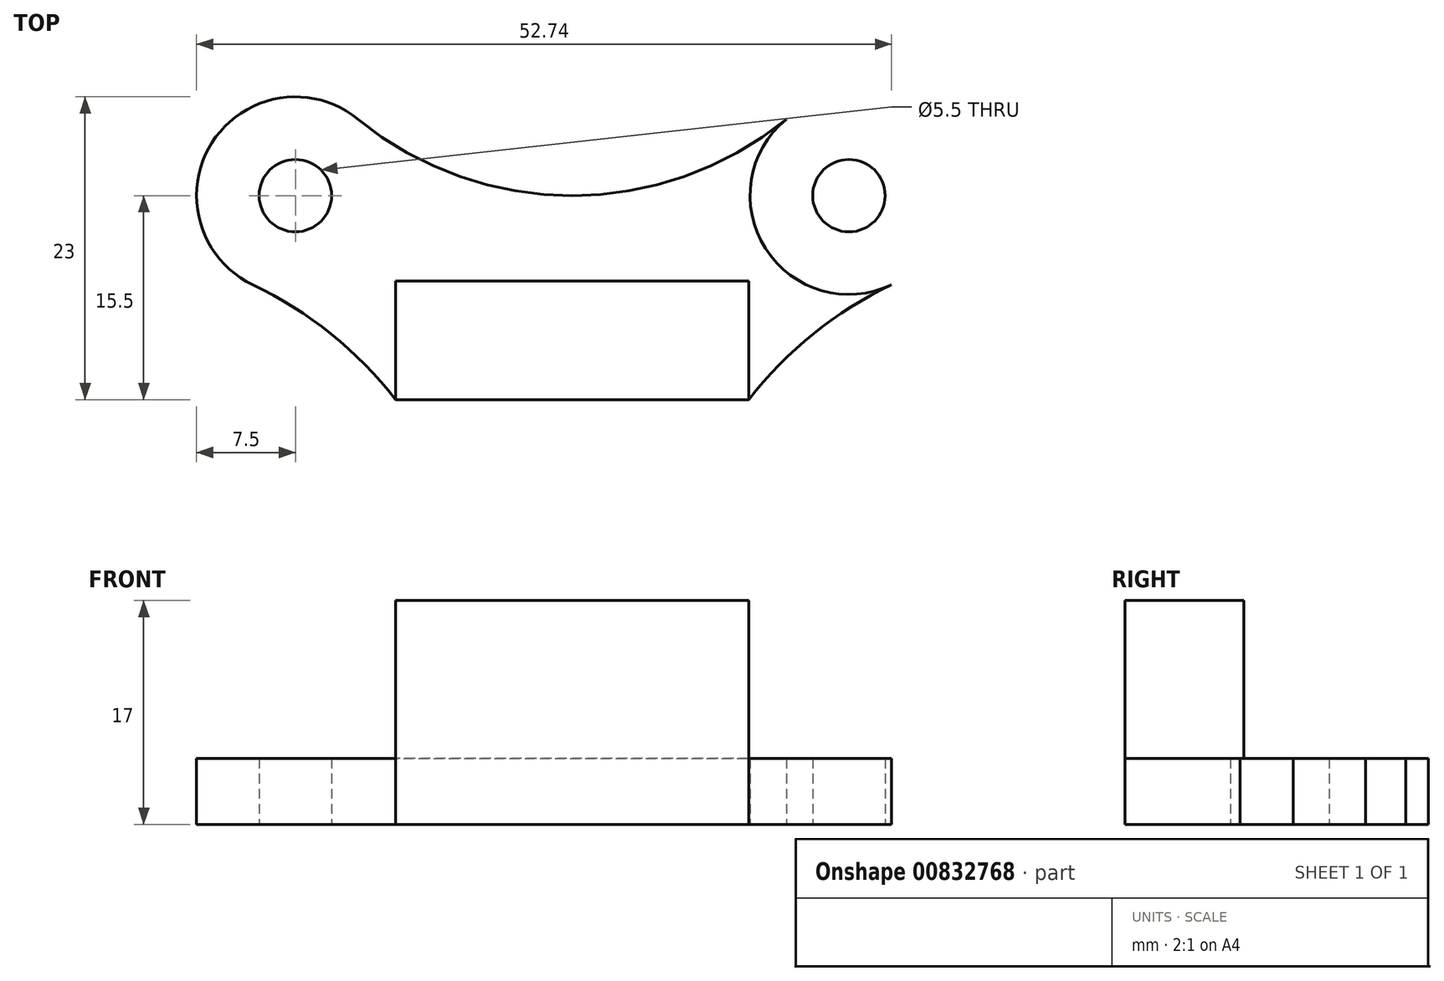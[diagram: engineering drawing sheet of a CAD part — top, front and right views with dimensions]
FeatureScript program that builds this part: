
annotation { "Feature Type Name" : "Feature", "Feature Type Description" : "" }
export const myFeature = defineFeature(function(context is Context, id is Id, definition is map)
    precondition{}
    {
        {
            var Q0;
            Q0=qCreatedBy(makeId("Top.planeOp"),FACE);
            var sketch = newSketch(context, id + "F0", { "sketchPlane" : qUnion([Q0])});
            skLineSegment(sketch, "E0", {"start": v(0, 0) * mm, "end": v(-21, 0) * mm, "construction": true});
            skLineSegment(sketch, "E1", {"start": v(0, 15.73) * mm, "end": v(0, -40) * mm, "construction": true});
            skCircle(sketch, "E2", {"center": v(-21, 0) * mm, "radius": 7.5 * mm});
            skCircle(sketch, "E3", {"center": v(-21, 0) * mm, "radius": 2.75 * mm});
            skCircle(sketch, "E4.MirrorC", {"center": v(21, 0) * mm, "radius": 7.5 * mm});
            skCircle(sketch, "E5.MirrorC", {"center": v(21, 0) * mm, "radius": 2.75 * mm});
            skLineSegment(sketch, "E6", {"start": v(-21, 0) * mm, "end": v(0, -40) * mm, "construction": true});
            skArc(sketch, "E7", {"start": v(-16.25, 5.8) * mm, "mid": v(0, 0) * mm, "end": v(16.25, 5.8) * mm});
            skCircle(sketch, "E8", {"center": v(0, -40) * mm, "radius": 7.5 * mm, "construction": true});
            skArc(sketch, "E9", {"start": v(-7.4, -38.82) * mm, "mid": v(-10.5, -20) * mm, "end": v(-24.24, -6.77) * mm});
            skArc(sketch, "E10.MirrorCS", {"start": v(7.4, -38.82) * mm, "mid": v(10.5, -20) * mm, "end": v(24.24, -6.77) * mm});
            skPoint(sketch, "E11", {"position": v(0, -6.5) * mm});
            skLineSegment(sketch, "E12", {"start": v(-13.4, -15.5) * mm, "end": v(13.4, -15.5) * mm});
            skSolve(sketch);
        }
        {
            var Q0;
            {var subQ4=sQuery(id+"F0.wireOp",EDGE,"E7");Q0=makeQuery(id+"F0.imprint","IMPRINT",FACE,{"disambiguationData":[TD([[makeQuery(id+"F0.imprint","IMPRINT",EDGE,{"derivedFrom":subQ4}),-1.0]])]});}
            var Q1;
            Q1=makeQuery(id+"F0.imprint","IMPRINT",FACE,{"disambiguationData":[TD([[makeQuery(id+"F0.imprint","IMPRINT",EDGE,{"derivedFrom":sQuery(id+"F0.wireOp",EDGE,"E3")}),-1.0]])]});
            var Q2;
            Q2=makeQuery(id+"F0.imprint","IMPRINT",FACE,{"disambiguationData":[TD([[makeQuery(id+"F0.imprint","IMPRINT",EDGE,{"derivedFrom":sQuery(id+"F0.wireOp",EDGE,"E5.MirrorC")}),1.0]])]});
            extrude(context, id + "F1", {"entities" : qUnion([Q0, Q1, Q2]), "depth" : 5 * mm, "offsetDistance" : 25 * mm});
        }
        {
            var Q0;
            Q0=makeQuery(id+"F1.opExtrude","CAP_FACE",FACE,{"disambiguationData":[OSD([sQuery(id+"F0.wireOp",EDGE,"E2"),sQuery(id+"F0.wireOp",EDGE,"E3"),sQuery(id+"F0.wireOp",EDGE,"E4.MirrorC"),sQuery(id+"F0.wireOp",EDGE,"E5.MirrorC"),sQuery(id+"F0.wireOp",EDGE,"E7"),sQuery(id+"F0.wireOp",EDGE,"E9"),sQuery(id+"F0.wireOp",EDGE,"E10.MirrorCS"),sQuery(id+"F0.wireOp",EDGE,"E12")])],"isStart":false});
            var sketch = newSketch(context, id + "F2", { "sketchPlane" : qUnion([Q0])});
            skLineSegment(sketch, "E13", {"start": v(0, 0) * mm, "end": v(0, -15.5) * mm, "construction": true});
            skPoint(sketch, "E14.0", {"position": v(0, -6.5) * mm});
            skLineSegment(sketch, "E15", {"start": v(0, -6.5) * mm, "end": v(-13.4, -6.5) * mm});
            skLineSegment(sketch, "E16", {"start": v(-13.4, -6.5) * mm, "end": v(-13.4, -15.5) * mm});
            skLineSegment(sketch, "E17.MirrorCS", {"start": v(0, -6.5) * mm, "end": v(13.4, -6.5) * mm});
            skLineSegment(sketch, "E18.MirrorCS", {"start": v(13.4, -6.5) * mm, "end": v(13.4, -15.5) * mm});
            skSolve(sketch);
        }
        {
            var Q0;
            Q0=makeQuery(id+"F2.imprint","IMPRINT",FACE,{"disambiguationData":[TD([[makeQuery(id+"F2.imprint","IMPRINT",EDGE,{"derivedFrom":sQuery(id+"F2.wireOp",EDGE,"E15")}),1.0]])]});
            extrude(context, id + "F3", {"entities" : qUnion([Q0]), "operationType" : NewBodyOperationType.ADD, "depth" : 12 * mm, "offsetDistance" : 25 * mm});
        }
    });
